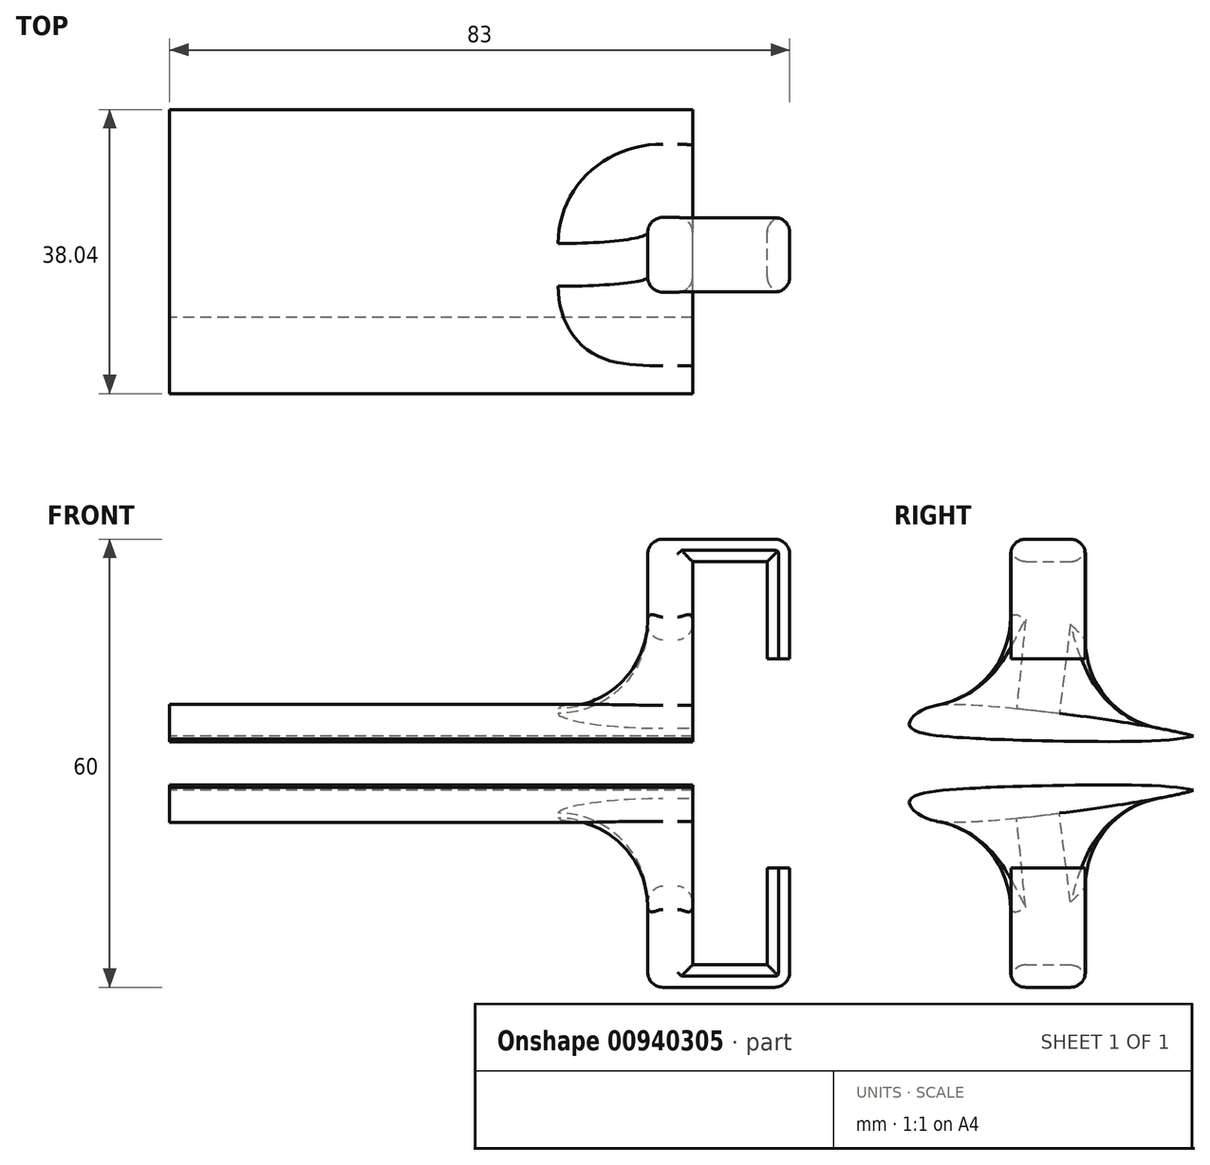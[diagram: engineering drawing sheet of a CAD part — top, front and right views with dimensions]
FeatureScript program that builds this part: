
annotation { "Feature Type Name" : "Feature", "Feature Type Description" : "" }
export const myFeature = defineFeature(function(context is Context, id is Id, definition is map)
    precondition{}
    {
        {
            var Q0;
            Q0=qCreatedBy(makeId("Right.planeOp"),FACE);
            var sketch = newSketch(context, id + "F0", { "sketchPlane" : qUnion([Q0])});
            skFitSpline(sketch, "E0", {"points": [v(-12.9, 9.76) * mm, v(-16.43, 6.84) * mm, v(-6.36, 5.24) * mm], "startDerivative": vector(-16.86, -3.07) * mm, "endDerivative": vector(12.46, -1.2) * mm});
            skFitSpline(sketch, "E1", {"points": [v(-12.9, 9.76) * mm, v(21.48, 5.63) * mm], "startDerivative": vector(14.1, 2.6) * mm, "endDerivative": vector(13.1, -4.41) * mm});
            skFitSpline(sketch, "E2", {"points": [v(-6.36, 5.24) * mm, v(21.48, 5.63) * mm], "startDerivative": vector(14.53, -0.44) * mm, "endDerivative": vector(11.41, 3.8) * mm});
            skSolve(sketch);
        }
        {
            var Q0;
            Q0=makeQuery(id+"F0.imprint","IMPRINT",FACE,{"disambiguationData":[TD([[makeQuery(id+"F0.imprint","IMPRINT",EDGE,{"derivedFrom":sQuery(id+"F0.wireOp",EDGE,"E0")}),1.0]])]});
            extrude(context, id + "F1", {"entities" : qUnion([Q0]), "depth" : 70 * mm, "offsetDistance" : 25 * mm});
        }
        {
            var Q0;
            Q0=qCreatedBy(makeId("Top.planeOp"),FACE);
            cPlane(context, id + "F2", {"entities" : qUnion([Q0]), "cplaneType" : CPlaneType.OFFSET, "offset" : 12 * mm, "width" : 150 * mm, "height" : 150 * mm});
        }
        {
            var Q0;
            Q0=qCreatedBy(id+"F2.planeOp",FACE);
            var sketch = newSketch(context, id + "F3", { "sketchPlane" : qUnion([Q0])});
            skFitSpline(sketch, "E3.0", {"points": [v(70, -12.9) * mm, v(70, -8.2) * mm, v(70, 17.11) * mm, v(70, 21.48) * mm]});
            skLineSegment(sketch, "E4.bottom", {"start": v(70, -2.98) * mm, "end": v(64, -2.98) * mm});
            skLineSegment(sketch, "E4.top", {"start": v(70, 7.02) * mm, "end": v(64, 7.02) * mm});
            skLineSegment(sketch, "E4.left", {"start": v(70, -2.98) * mm, "end": v(70, 7.02) * mm});
            skLineSegment(sketch, "E4.right", {"start": v(64, -2.98) * mm, "end": v(64, 7.02) * mm});
            skSolve(sketch);
        }
        {
            var Q0;
            {var subQ2=sQuery(id+"F3.wireOp",EDGE,"E4.bottom");Q0=makeQuery(id+"F3.imprint","IMPRINT",FACE,{"disambiguationData":[TD([[makeQuery(id+"F3.imprint","IMPRINT",EDGE,{"derivedFrom":subQ2}),-1.0]])]});}
            extrude(context, id + "F4", {"entities" : qUnion([Q0]), "operationType" : NewBodyOperationType.ADD, "oppositeDirection" : true, "depth" : 6 * mm, "offsetDistance" : 25 * mm});
        }
        {
            var Q0;
            Q0=makeQuery(id+"F4.opExtrude","CAP_FACE",FACE,{"disambiguationData":[OSD([sQuery(id+"F3.wireOp",EDGE,"E3.0"),sQuery(id+"F3.wireOp",EDGE,"E4.bottom"),sQuery(id+"F3.wireOp",EDGE,"E4.top"),sQuery(id+"F3.wireOp",EDGE,"E4.right")])],"isStart":true});
            extrude(context, id + "F5", {"entities" : qUnion([Q0]), "operationType" : NewBodyOperationType.ADD, "depth" : 20 * mm, "offsetDistance" : 25 * mm});
        }
        {
            var Q0;
            {var subQ0=sQuery(id+"F3.wireOp",EDGE,"E3.0");Q0=makeQuery(id+"F5.boolean.opBoolean","MERGE",FACE,{"derivedFrom":[makeQuery(id+"F4.boolean.opBoolean","MERGE",FACE,{"derivedFrom":[makeQuery(id+"F1.opExtrude","CAP_FACE",FACE,{"disambiguationData":[OSD([sQuery(id+"F0.wireOp",EDGE,"E0"),sQuery(id+"F0.wireOp",EDGE,"E1"),sQuery(id+"F0.wireOp",EDGE,"E2")])],"isStart":false}),makeQuery(id+"F4.opExtrude","SWEPT_FACE",FACE,{"disambiguationData":[OSD([subQ0])]})]}),makeQuery(id+"F5.opExtrude","SWEPT_FACE",FACE,{"disambiguationData":[OSD([subQ0])]})]});}
            var sketch = newSketch(context, id + "F6", { "sketchPlane" : qUnion([Q0])});
            skLineSegment(sketch, "E5", {"start": v(-2.98, 29) * mm, "end": v(7.02, 29) * mm});
            skSolve(sketch);
        }
        {
            var Q0;
            {var subQ0=sQuery(id+"F6.wireOp",EDGE,"E5");Q0=makeQuery(id+"F6.imprint","IMPRINT",FACE,{"disambiguationData":[TD([[makeQuery(id+"F6.imprint","IMPRINT",EDGE,{"derivedFrom":subQ0}),1.0]])]});}
            extrude(context, id + "F7", {"entities" : qUnion([Q0]), "operationType" : NewBodyOperationType.ADD, "depth" : 13 * mm, "offsetDistance" : 25 * mm});
        }
        {
            var Q0;
            Q0=makeQuery(id+"F7.opExtrude","SWEPT_FACE",FACE,{"disambiguationData":[OSD([sQuery(id+"F6.wireOp",EDGE,"E5")])]});
            var sketch = newSketch(context, id + "F8", { "sketchPlane" : qUnion([Q0])});
            skLineSegment(sketch, "E6", {"start": v(80, 2.98) * mm, "end": v(80, -7.02) * mm});
            skSolve(sketch);
        }
        {
            var Q0;
            {var subQ0=sQuery(id+"F8.wireOp",EDGE,"E6");Q0=makeQuery(id+"F8.imprint","IMPRINT",FACE,{"disambiguationData":[TD([[makeQuery(id+"F8.imprint","IMPRINT",EDGE,{"derivedFrom":subQ0}),1.0]])]});}
            extrude(context, id + "F9", {"entities" : qUnion([Q0]), "operationType" : NewBodyOperationType.ADD, "depth" : 13 * mm, "offsetDistance" : 25 * mm});
        }
        {
            var Q0;
            {var subQ0=sQuery(id+"F3.wireOp",EDGE,"E4.bottom");var subQ1=sQuery(id+"F3.wireOp",EDGE,"E3.0");Q0=makeQuery(id+"F5.boolean.opBoolean","MERGE",EDGE,{"derivedFrom":[makeQuery(id+"F4.opExtrude","SWEPT_EDGE",EDGE,{"disambiguationData":[OSD([subQ1,subQ0])]}),makeQuery(id+"F5.opExtrude","SWEPT_EDGE",EDGE,{"disambiguationData":[OSD([subQ1,subQ0])]})]});}
            var Q1;
            Q1=makeQuery(id+"F7.opExtrude","SWEPT_EDGE",EDGE,{"disambiguationData":[OSD([sQuery(id+"F3.wireOp",EDGE,"E3.0"),sQuery(id+"F3.wireOp",EDGE,"E4.bottom"),sQuery(id+"F6.wireOp",EDGE,"E5")])]});
            var Q2;
            Q2=makeQuery(id+"F9.opExtrude","SWEPT_EDGE",EDGE,{"disambiguationData":[OSD([sQuery(id+"F3.wireOp",EDGE,"E3.0"),sQuery(id+"F3.wireOp",EDGE,"E4.bottom"),sQuery(id+"F6.wireOp",EDGE,"E5"),sQuery(id+"F8.wireOp",EDGE,"E6")])]});
            var Q3;
            Q3=makeQuery(id+"F9.opExtrude","SWEPT_EDGE",EDGE,{"disambiguationData":[OSD([sQuery(id+"F3.wireOp",EDGE,"E3.0"),sQuery(id+"F3.wireOp",EDGE,"E4.top"),sQuery(id+"F6.wireOp",EDGE,"E5"),sQuery(id+"F8.wireOp",EDGE,"E6")])]});
            var Q4;
            Q4=makeQuery(id+"F9.opExtrude","CAP_EDGE",EDGE,{"disambiguationData":[OSD([sQuery(id+"F8.wireOp",EDGE,"E6")])],"isStart":true});
            var Q5;
            Q5=makeQuery(id+"F7.opExtrude","SWEPT_EDGE",EDGE,{"disambiguationData":[OSD([sQuery(id+"F3.wireOp",EDGE,"E3.0"),sQuery(id+"F3.wireOp",EDGE,"E4.top"),sQuery(id+"F6.wireOp",EDGE,"E5")])]});
            var Q6;
            {var subQ0=sQuery(id+"F3.wireOp",EDGE,"E4.top");var subQ1=sQuery(id+"F3.wireOp",EDGE,"E3.0");Q6=makeQuery(id+"F5.boolean.opBoolean","MERGE",EDGE,{"derivedFrom":[makeQuery(id+"F4.opExtrude","SWEPT_EDGE",EDGE,{"disambiguationData":[OSD([subQ1,subQ0])]}),makeQuery(id+"F5.opExtrude","SWEPT_EDGE",EDGE,{"disambiguationData":[OSD([subQ1,subQ0])]})]});}
            var Q7;
            Q7=makeQuery(id+"F7.opExtrude","CAP_EDGE",EDGE,{"disambiguationData":[OSD([sQuery(id+"F6.wireOp",EDGE,"E5")])],"isStart":true});
            var Q8;
            {var subQ0=sQuery(id+"F3.wireOp",EDGE,"E4.top");Q8=makeQuery(id+"F7.boolean.opBoolean","MERGE",EDGE,{"derivedFrom":[makeQuery(id+"F5.opExtrude","CAP_EDGE",EDGE,{"disambiguationData":[OSD([subQ0])],"isStart":false}),makeQuery(id+"F7.opExtrude","SWEPT_EDGE",EDGE,{"disambiguationData":[OSD([sQuery(id+"F3.wireOp",EDGE,"E3.0"),subQ0])]})]});}
            var Q9;
            {var subQ0=sQuery(id+"F3.wireOp",EDGE,"E4.top");var subQ1=sQuery(id+"F3.wireOp",EDGE,"E3.0");Q9=makeQuery(id+"F9.boolean.opBoolean","MERGE",EDGE,{"derivedFrom":[makeQuery(id+"F7.opExtrude","CAP_EDGE",EDGE,{"disambiguationData":[OSD([subQ1,subQ0])],"isStart":false}),makeQuery(id+"F9.opExtrude","SWEPT_EDGE",EDGE,{"disambiguationData":[OSD([subQ1,subQ0,sQuery(id+"F6.wireOp",EDGE,"E5")])]})]});}
            var Q10;
            {var subQ0=sQuery(id+"F3.wireOp",EDGE,"E4.bottom");var subQ1=sQuery(id+"F3.wireOp",EDGE,"E3.0");Q10=makeQuery(id+"F9.boolean.opBoolean","MERGE",EDGE,{"derivedFrom":[makeQuery(id+"F7.opExtrude","CAP_EDGE",EDGE,{"disambiguationData":[OSD([subQ1,subQ0])],"isStart":false}),makeQuery(id+"F9.opExtrude","SWEPT_EDGE",EDGE,{"disambiguationData":[OSD([subQ1,subQ0,sQuery(id+"F6.wireOp",EDGE,"E5")])]})]});}
            var Q11;
            Q11=makeQuery(id+"F7.opExtrude","CAP_EDGE",EDGE,{"disambiguationData":[OSD([sQuery(id+"F3.wireOp",EDGE,"E3.0")])],"isStart":false});
            var Q12;
            {var subQ0=sQuery(id+"F3.wireOp",EDGE,"E4.bottom");Q12=makeQuery(id+"F7.boolean.opBoolean","MERGE",EDGE,{"derivedFrom":[makeQuery(id+"F5.opExtrude","CAP_EDGE",EDGE,{"disambiguationData":[OSD([subQ0])],"isStart":false}),makeQuery(id+"F7.opExtrude","SWEPT_EDGE",EDGE,{"disambiguationData":[OSD([sQuery(id+"F3.wireOp",EDGE,"E3.0"),subQ0])]})]});}
            var Q13;
            Q13=makeQuery(id+"F5.opExtrude","CAP_EDGE",EDGE,{"disambiguationData":[OSD([sQuery(id+"F3.wireOp",EDGE,"E4.right")])],"isStart":false});
            var Q14;
            {var subQ0=sQuery(id+"F3.wireOp",EDGE,"E4.right");var subQ1=sQuery(id+"F3.wireOp",EDGE,"E4.bottom");Q14=makeQuery(id+"F5.boolean.opBoolean","MERGE",EDGE,{"derivedFrom":[makeQuery(id+"F4.opExtrude","SWEPT_EDGE",EDGE,{"disambiguationData":[OSD([subQ1,subQ0])]}),makeQuery(id+"F5.opExtrude","SWEPT_EDGE",EDGE,{"disambiguationData":[OSD([subQ1,subQ0])]})]});}
            var Q15;
            {var subQ0=sQuery(id+"F3.wireOp",EDGE,"E4.right");var subQ1=sQuery(id+"F3.wireOp",EDGE,"E4.top");Q15=makeQuery(id+"F5.boolean.opBoolean","MERGE",EDGE,{"derivedFrom":[makeQuery(id+"F4.opExtrude","SWEPT_EDGE",EDGE,{"disambiguationData":[OSD([subQ1,subQ0])]}),makeQuery(id+"F5.opExtrude","SWEPT_EDGE",EDGE,{"disambiguationData":[OSD([subQ1,subQ0])]})]});}
            fillet(context, id + "F10", {"entities" : qUnion([Q0, Q1, Q2, Q3, Q4, Q5, Q6, Q7, Q8, Q9, Q10, Q11, Q12, Q13, Q14, Q15]), "radius" : 2 * mm, "tangentPropagation" : true, "allowEdgeOverflow" : false});
        }
        {
            var Q0;
            Q0=makeQuery(id+"F4.boolean.opBoolean","INTERSECT",EDGE,{"derivedFrom":[makeQuery(id+"F1.opExtrude","SWEPT_FACE",FACE,{"disambiguationData":[OSD([sQuery(id+"F0.wireOp",EDGE,"E1")])]}),makeQuery(id+"F4.opExtrude","SWEPT_FACE",FACE,{"disambiguationData":[OSD([sQuery(id+"F3.wireOp",EDGE,"E4.right")])]})]});
            var Q1;
            Q1=makeQuery(id+"F4.boolean.opBoolean","INTERSECT",EDGE,{"derivedFrom":[makeQuery(id+"F1.opExtrude","SWEPT_FACE",FACE,{"disambiguationData":[OSD([sQuery(id+"F0.wireOp",EDGE,"E1")])]}),makeQuery(id+"F4.opExtrude","SWEPT_FACE",FACE,{"disambiguationData":[OSD([sQuery(id+"F3.wireOp",EDGE,"E4.bottom")])]})]});
            var Q2;
            Q2=makeQuery(id+"F4.boolean.opBoolean","INTERSECT",EDGE,{"derivedFrom":[makeQuery(id+"F1.opExtrude","SWEPT_FACE",FACE,{"disambiguationData":[OSD([sQuery(id+"F0.wireOp",EDGE,"E1")])]}),makeQuery(id+"F4.opExtrude","SWEPT_FACE",FACE,{"disambiguationData":[OSD([sQuery(id+"F3.wireOp",EDGE,"E4.top")])]})]});
            fillet(context, id + "F11", {"entities" : qUnion([Q0, Q1, Q2]), "radius" : 12 * mm, "tangentPropagation" : true, "allowEdgeOverflow" : false});
        }
        {
            var Q0;
            Q0=qCreatedBy(id+"F2.planeOp",FACE);
            cPlane(context, id + "F12", {"entities" : qUnion([Q0]), "cplaneType" : CPlaneType.OFFSET, "offset" : 10 * mm, "oppositeDirection" : true, "width" : 150 * mm, "height" : 150 * mm});
        }
        {
            var Q0;
            Q0=makeQuery(id+"F1.opExtrude","SWEPT_BODY",BODY,{"disambiguationData":[OSD([sQuery(id+"F0.wireOp",EDGE,"E0"),sQuery(id+"F0.wireOp",EDGE,"E1"),sQuery(id+"F0.wireOp",EDGE,"E2")])]});
            var Q1;
            Q1=qCreatedBy(id+"F12.planeOp",FACE);
            mirror(context, id + "F13", {"entities" : qUnion([Q0]), "mirrorPlane" : qUnion([Q1])});
        }
    });
